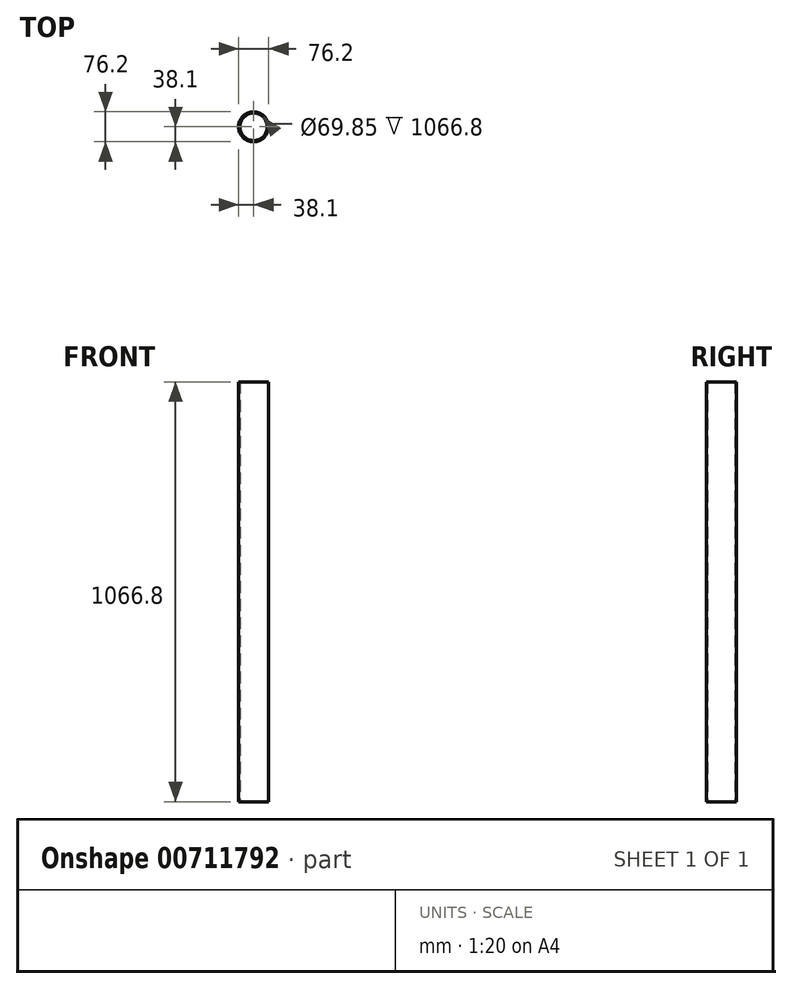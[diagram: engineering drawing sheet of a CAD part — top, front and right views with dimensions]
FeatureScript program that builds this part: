
annotation { "Feature Type Name" : "Feature", "Feature Type Description" : "" }
export const myFeature = defineFeature(function(context is Context, id is Id, definition is map)
    precondition{}
    {
        {
            var Q0;
            Q0=qCreatedBy(makeId("Top.planeOp"),FACE);
            var sketch = newSketch(context, id + "F0", { "sketchPlane" : qUnion([Q0])});
            skCircle(sketch, "E0", {"center": v(0, 0) * mm, "radius": 38.1 * mm});
            skCircle(sketch, "E1", {"center": v(0, 0) * mm, "radius": 34.93 * mm});
            skSolve(sketch);
        }
        {
            var Q0;
            Q0 = qSketchRegion(id + "F0", true);
            extrude(context, id + "F1", {"entities" : qUnion([Q0]), "endBound" : BoundingType.SYMMETRIC, "depth" : 1066.8 * mm, "offsetDistance" : 25.4 * mm});
        }
    });
